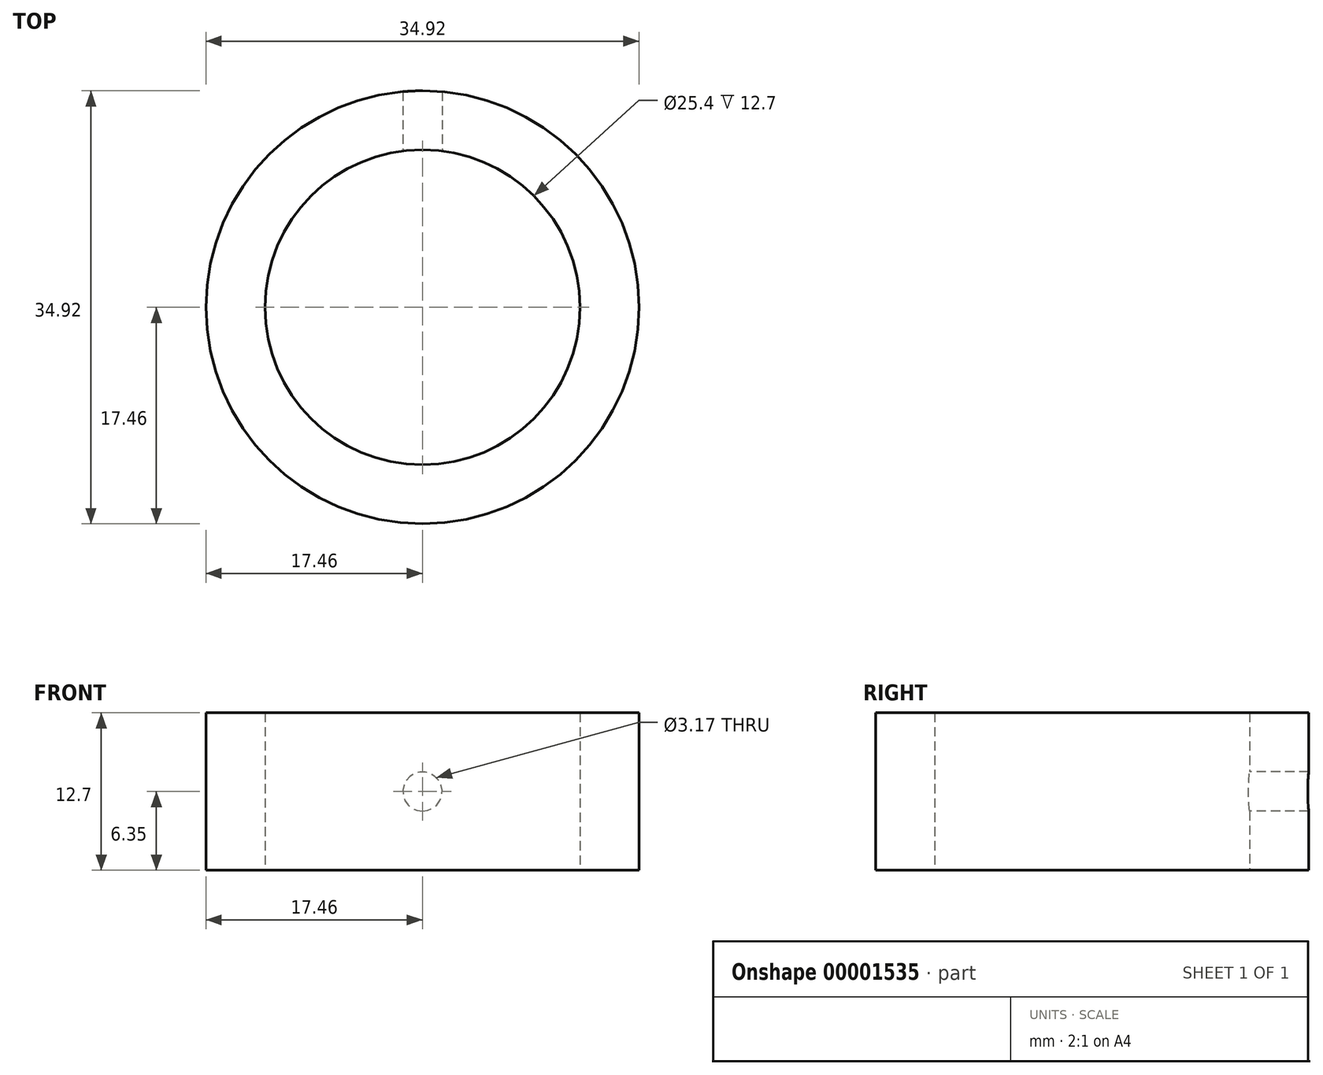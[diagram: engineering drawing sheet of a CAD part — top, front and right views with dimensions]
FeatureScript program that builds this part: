
annotation { "Feature Type Name" : "Feature", "Feature Type Description" : "" }
export const myFeature = defineFeature(function(context is Context, id is Id, definition is map)
    precondition{}
    {
        {
            var Q0;
            Q0=qCreatedBy(makeId("Top.planeOp"),FACE);
            var sketch = newSketch(context, id + "F0", { "sketchPlane" : qUnion([Q0])});
            skCircle(sketch, "E0", {"center": v(0, 0) * mm, "radius": 12.7 * mm});
            skCircle(sketch, "E1", {"center": v(0, 0) * mm, "radius": 17.46 * mm});
            skSolve(sketch);
        }
        {
            var Q0;
            Q0=makeQuery(id+"F0.imprint","IMPRINT",FACE,{"disambiguationData":[TD([[makeQuery(id+"F0.imprint","IMPRINT",EDGE,{"derivedFrom":sQuery(id+"F0.wireOp",EDGE,"E0")}),-1.0]])]});
            extrude(context, id + "F1", {"entities" : qUnion([Q0]), "depth" : 12.7 * mm});
        }
        {
            var Q0;
            Q0=qCreatedBy(makeId("Front.planeOp"),FACE);
            var sketch = newSketch(context, id + "F2", { "sketchPlane" : qUnion([Q0])});
            skCircle(sketch, "E2", {"center": v(0, 6.35) * mm, "radius": 1.59 * mm});
            skSolve(sketch);
        }
        {
            var Q0;
            Q0=makeQuery(id+"F2.imprint","IMPRINT",FACE,{"disambiguationData":[TD([[makeQuery(id+"F2.imprint","IMPRINT",EDGE,{"derivedFrom":sQuery(id+"F2.wireOp",EDGE,"E2")}),1.0]])]});
            extrude(context, id + "F3", {"entities" : qUnion([Q0]), "operationType" : NewBodyOperationType.REMOVE, "oppositeDirection" : true, "depth" : 25.4 * mm});
        }
    });
